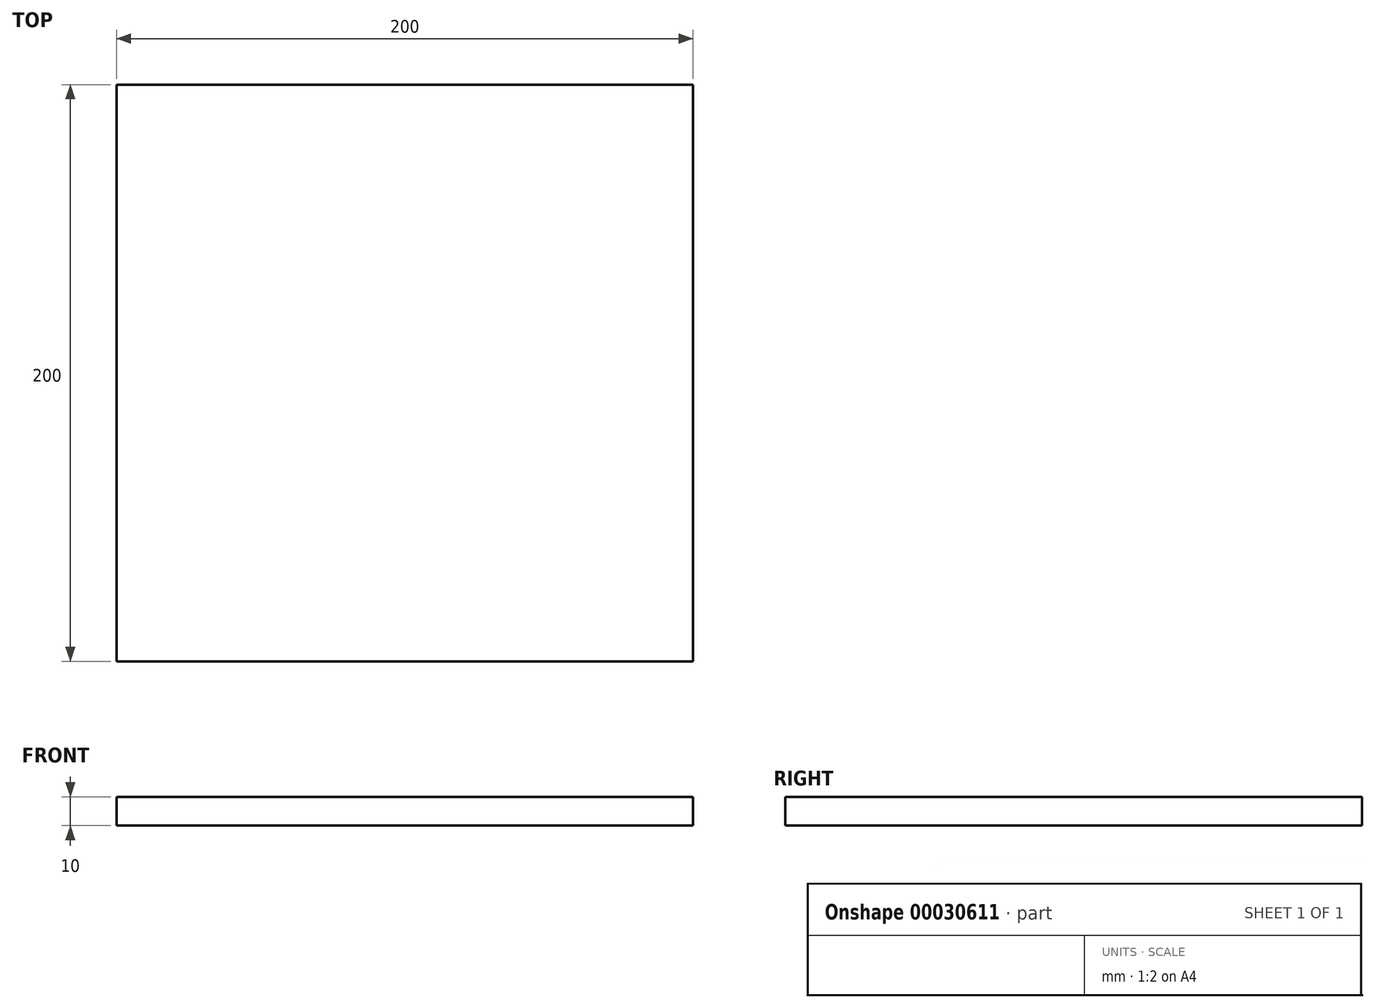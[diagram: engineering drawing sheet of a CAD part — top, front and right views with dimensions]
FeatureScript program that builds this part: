
annotation { "Feature Type Name" : "Feature", "Feature Type Description" : "" }
export const myFeature = defineFeature(function(context is Context, id is Id, definition is map)
    precondition{}
    {
        {
            var Q0;
            Q0=qCreatedBy(makeId("Top.planeOp"),FACE);
            var sketch = newSketch(context, id + "F0", { "sketchPlane" : qUnion([Q0])});
            skLineSegment(sketch, "E0.bottom", {"start": v(0, 0) * mm, "end": v(200, 0) * mm});
            skLineSegment(sketch, "E0.top", {"start": v(0, 200) * mm, "end": v(200, 200) * mm});
            skLineSegment(sketch, "E0.left", {"start": v(0, 0) * mm, "end": v(0, 200) * mm});
            skLineSegment(sketch, "E0.right", {"start": v(200, 0) * mm, "end": v(200, 200) * mm});
            skSolve(sketch);
        }
        {
            var Q0;
            Q0=makeQuery(id+"F0.imprint","IMPRINT",FACE,{"disambiguationData":[TD([[makeQuery(id+"F0.imprint","IMPRINT",EDGE,{"derivedFrom":sQuery(id+"F0.wireOp",EDGE,"E0.bottom")}),1.0]])]});
            extrude(context, id + "F1", {"entities" : qUnion([Q0]), "depth" : 10 * mm});
        }
    });
